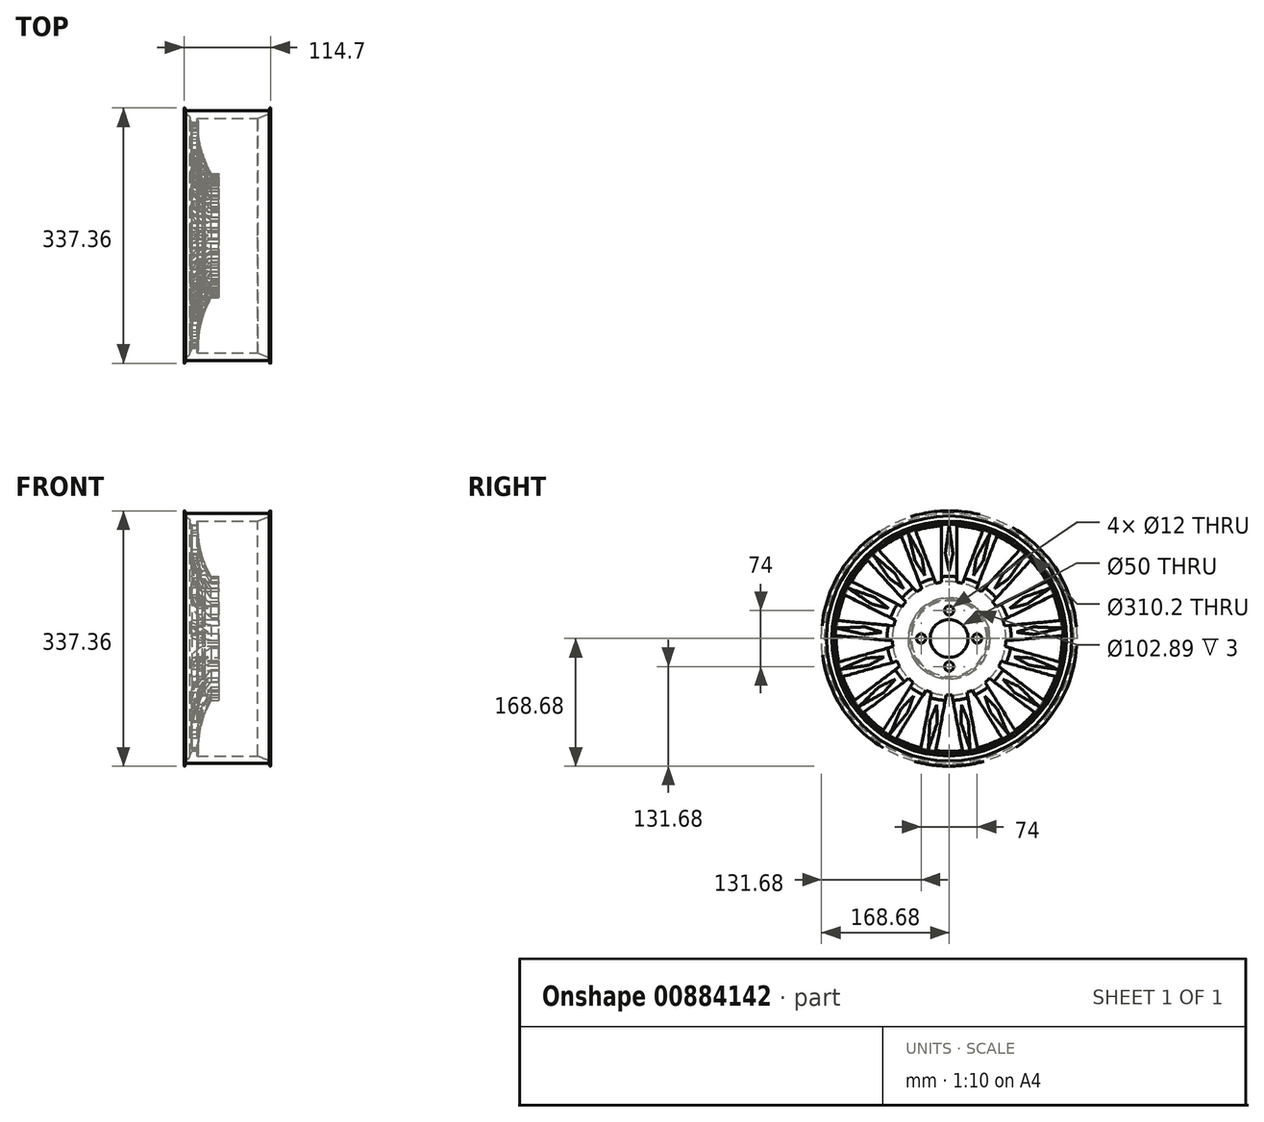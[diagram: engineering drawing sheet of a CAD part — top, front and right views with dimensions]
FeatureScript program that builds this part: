
annotation { "Feature Type Name" : "Feature", "Feature Type Description" : "" }
export const myFeature = defineFeature(function(context is Context, id is Id, definition is map)
    precondition{}
    {
        {
            var Q0;
            Q0=qCreatedBy(makeId("Front.planeOp"),FACE);
            var sketch = newSketch(context, id + "F0", { "sketchPlane" : qUnion([Q0])});
            skLineSegment(sketch, "E0", {"start": v(0, 0) * mm, "end": v(0, 165.1) * mm, "construction": true});
            skLineSegment(sketch, "E1", {"start": v(0, 0) * mm, "end": v(-35, 0) * mm, "construction": true});
            skLineSegment(sketch, "E2", {"start": v(0, 165.1) * mm, "end": v(-55, 165.1) * mm});
            skLineSegment(sketch, "E3", {"start": v(-35, 0) * mm, "end": v(-35, 25) * mm, "construction": true});
            skLineSegment(sketch, "E4", {"start": v(-35, 25) * mm, "end": v(-39.8, 25) * mm});
            skLineSegment(sketch, "E5", {"start": v(-40, 25.2) * mm, "end": v(-40, 49.8) * mm});
            skLineSegment(sketch, "E6", {"start": v(-39.8, 50) * mm, "end": v(-31.06, 50) * mm});
            skLineSegment(sketch, "E7", {"start": v(-55, 165.1) * mm, "end": v(-56.17, 168.55) * mm});
            skLineSegment(sketch, "E8", {"start": v(-56.39, 168.68) * mm, "end": v(-56.92, 168.6) * mm});
            skLineSegment(sketch, "E9", {"start": v(-57.34, 168.03) * mm, "end": v(-56.72, 163.88) * mm});
            skLineSegment(sketch, "E10", {"start": v(-56.67, 163.14) * mm, "end": v(-56.67, 162.14) * mm});
            skLineSegment(sketch, "E11", {"start": v(-56.41, 161.7) * mm, "end": v(-52.07, 159.23) * mm});
            skLineSegment(sketch, "E12", {"start": v(-49.55, 154.88) * mm, "end": v(-49.55, 153.88) * mm});
            skLineSegment(sketch, "E13", {"start": v(-49.16, 152.7) * mm, "end": v(-46.66, 149.26) * mm});
            skArc(sketch, "E14", {"start": v(-46.66, 149.26) * mm, "mid": v(-45.48, 111.09) * mm, "end": v(-32.98, 75) * mm});
            skPoint(sketch, "E15.visualSharp", {"position": v(-56.22, 168.7) * mm});
            skArc(sketch, "E15.filletArc", {"start": v(-56.17, 168.55) * mm, "mid": v(-56.25, 168.66) * mm, "end": v(-56.39, 168.68) * mm});
            skPoint(sketch, "E16.visualSharp", {"position": v(-57.42, 168.53) * mm});
            skArc(sketch, "E16.filletArc", {"start": v(-56.92, 168.6) * mm, "mid": v(-57.25, 168.4) * mm, "end": v(-57.34, 168.03) * mm});
            skPoint(sketch, "E17.visualSharp", {"position": v(-56.67, 163.51) * mm});
            skArc(sketch, "E17.filletArc", {"start": v(-56.67, 163.14) * mm, "mid": v(-56.68, 163.5) * mm, "end": v(-56.72, 163.88) * mm});
            skPoint(sketch, "E18.visualSharp", {"position": v(-56.67, 161.85) * mm});
            skArc(sketch, "E18.filletArc", {"start": v(-56.67, 162.14) * mm, "mid": v(-56.6, 161.89) * mm, "end": v(-56.41, 161.7) * mm});
            skPoint(sketch, "E19.visualSharp", {"position": v(-49.55, 157.79) * mm});
            skArc(sketch, "E19.filletArc", {"start": v(-49.55, 154.88) * mm, "mid": v(-50.22, 157.4) * mm, "end": v(-52.07, 159.23) * mm});
            skPoint(sketch, "E20.visualSharp", {"position": v(-49.55, 153.23) * mm});
            skArc(sketch, "E20.filletArc", {"start": v(-49.55, 153.88) * mm, "mid": v(-49.45, 153.26) * mm, "end": v(-49.16, 152.7) * mm});
            skPoint(sketch, "E21.visualSharp", {"position": v(-32.27, 50) * mm});
            skArc(sketch, "E21.filletArc", {"start": v(-31.06, 50) * mm, "mid": v(-29.86, 53.61) * mm, "end": v(-32.98, 51.45) * mm});
            skLineSegment(sketch, "E22", {"start": v(0, 155.1) * mm, "end": v(-40, 155.1) * mm});
            skLineSegment(sketch, "E23", {"start": v(-40, 155.1) * mm, "end": v(-39.2, 153.27) * mm});
            skLineSegment(sketch, "E24", {"start": v(-39.2, 153.27) * mm, "end": v(-38.39, 151.44) * mm});
            skLineSegment(sketch, "E25", {"start": v(-32.98, 75) * mm, "end": v(-29.98, 75) * mm});
            skLineSegment(sketch, "E26", {"start": v(-29.98, 75) * mm, "end": v(-29.98, 51.45) * mm});
            skLineSegment(sketch, "E27", {"start": v(-29.98, 51.45) * mm, "end": v(-32.98, 51.45) * mm});
            skLineSegment(sketch, "E28", {"start": v(-11.34, 82.01) * mm, "end": v(-11.34, 0) * mm});
            skLineSegment(sketch, "E29", {"start": v(-35, 25) * mm, "end": v(-11.34, 25) * mm});
            skLineSegment(sketch, "E30", {"start": v(-11.34, 82.01) * mm, "end": v(-21.34, 82.01) * mm});
            skArc(sketch, "E31", {"start": v(-38.39, 151.44) * mm, "mid": v(-34.96, 115.48) * mm, "end": v(-21.34, 82.01) * mm});
            skLineSegment(sketch, "E32.MirrorCS", {"start": v(0, 165.1) * mm, "end": v(55, 165.1) * mm});
            skLineSegment(sketch, "E33.MirrorCS", {"start": v(55, 165.1) * mm, "end": v(56.17, 168.55) * mm});
            skArc(sketch, "E34.MirrorCS", {"start": v(56.17, 168.55) * mm, "mid": v(56.25, 168.66) * mm, "end": v(56.39, 168.68) * mm});
            skLineSegment(sketch, "E35.MirrorCS", {"start": v(56.39, 168.68) * mm, "end": v(56.92, 168.6) * mm});
            skArc(sketch, "E36.MirrorCS", {"start": v(56.92, 168.6) * mm, "mid": v(57.25, 168.4) * mm, "end": v(57.34, 168.03) * mm});
            skLineSegment(sketch, "E37.MirrorCS", {"start": v(57.34, 168.03) * mm, "end": v(56.72, 163.88) * mm});
            skArc(sketch, "E38.MirrorCS", {"start": v(56.67, 163.14) * mm, "mid": v(56.68, 163.5) * mm, "end": v(56.72, 163.88) * mm});
            skLineSegment(sketch, "E39.MirrorCS", {"start": v(56.67, 163.14) * mm, "end": v(56.67, 162.14) * mm});
            skArc(sketch, "E40.MirrorCS", {"start": v(56.67, 162.14) * mm, "mid": v(56.65, 162) * mm, "end": v(56.6, 161.89) * mm});
            skLineSegment(sketch, "E41.MirrorCS", {"start": v(0, 155.1) * mm, "end": v(40, 155.1) * mm});
            skLineSegment(sketch, "E42", {"start": v(40, 155.1) * mm, "end": v(56.6, 161.89) * mm});
            skPoint(sketch, "E43.orphan", {"position": v(56.41, 161.7) * mm});
            skPoint(sketch, "E44.visualSharp", {"position": v(-40, 50) * mm});
            skArc(sketch, "E44.filletArc", {"start": v(-39.8, 50) * mm, "mid": v(-39.94, 49.95) * mm, "end": v(-40, 49.8) * mm});
            skPoint(sketch, "E45.visualSharp", {"position": v(-40, 25) * mm});
            skArc(sketch, "E45.filletArc", {"start": v(-40, 25.2) * mm, "mid": v(-39.94, 25.06) * mm, "end": v(-39.8, 25) * mm});
            skSolve(sketch);
        }
        {
            var Q0;
            Q0 = qSketchRegion(id + "F0", true);
            var Q1;
            Q1=sQuery(id+"F0.wireOp",EDGE,"E1");
            revolve(context, id + "F1", {"surfaceOperationType" : NewSurfaceOperationType.NEW, "entities" : qUnion([Q0]), "axis" : qUnion([Q1]), "revolveType" : RevolveType.FULL});
        }
        {
            var Q0;
            Q0=makeQuery(id+"F1.opRevolve","SWEPT_FACE",FACE,{"disambiguationData":[OSD([sQuery(id+"F0.wireOp",EDGE,"E5")])]});
            var sketch = newSketch(context, id + "F2", { "sketchPlane" : qUnion([Q0])});
            skLineSegment(sketch, "E46", {"start": v(0, 89.26) * mm, "end": v(0, 149.26) * mm, "construction": true});
            skLineSegment(sketch, "E47", {"start": v(10, 74.33) * mm, "end": v(10, 148.93) * mm});
            skLineSegment(sketch, "E48.MirrorCS", {"start": v(-10, 74.33) * mm, "end": v(-10, 148.93) * mm});
            skLineSegment(sketch, "E49", {"start": v(5, 79.84) * mm, "end": v(5, 144.18) * mm, "construction": true});
            skLineSegment(sketch, "E50.MirrorCS", {"start": v(-5, 79.84) * mm, "end": v(-5, 144.18) * mm, "construction": true});
            skLineSegment(sketch, "E51", {"start": v(0, 89.26) * mm, "end": v(5, 112.01) * mm});
            skLineSegment(sketch, "E52", {"start": v(5, 112.01) * mm, "end": v(0, 149.26) * mm});
            skLineSegment(sketch, "E53", {"start": v(0, 89.26) * mm, "end": v(-5, 112.01) * mm});
            skLineSegment(sketch, "E54", {"start": v(-5, 112.01) * mm, "end": v(0, 149.26) * mm});
            skCircle(sketch, "E55", {"center": v(0, 0) * mm, "radius": 75 * mm});
            skCircle(sketch, "E56", {"center": v(0, 0) * mm, "radius": 149.26 * mm});
            skLineSegment(sketch, "E57.1.0", {"start": v(-36.18, 65.7) * mm, "end": v(-63.12, 135.26) * mm});
            skLineSegment(sketch, "E57.1.1", {"start": v(-35.8, 106.25) * mm, "end": v(-53.92, 139.18) * mm});
            skLineSegment(sketch, "E57.1.2", {"start": v(-32.25, 83.24) * mm, "end": v(-35.8, 106.25) * mm});
            skLineSegment(sketch, "E57.1.3", {"start": v(-32.25, 83.24) * mm, "end": v(-45.13, 102.64) * mm});
            skLineSegment(sketch, "E57.1.4", {"start": v(-45.13, 102.64) * mm, "end": v(-53.92, 139.18) * mm});
            skLineSegment(sketch, "E57.1.5", {"start": v(-17.53, 72.92) * mm, "end": v(-44.47, 142.48) * mm});
            skLineSegment(sketch, "E57.2.0", {"start": v(-57.47, 48.2) * mm, "end": v(-107.72, 103.32) * mm});
            skLineSegment(sketch, "E57.2.1", {"start": v(-71.77, 86.15) * mm, "end": v(-100.56, 110.3) * mm});
            skLineSegment(sketch, "E57.2.2", {"start": v(-60.14, 65.97) * mm, "end": v(-71.77, 86.15) * mm});
            skLineSegment(sketch, "E57.2.3", {"start": v(-60.14, 65.97) * mm, "end": v(-79.16, 79.4) * mm});
            skLineSegment(sketch, "E57.2.4", {"start": v(-79.16, 79.4) * mm, "end": v(-100.56, 110.3) * mm});
            skLineSegment(sketch, "E57.2.5", {"start": v(-42.69, 61.67) * mm, "end": v(-92.94, 116.8) * mm});
            skLineSegment(sketch, "E57.3.0", {"start": v(-71, 24.18) * mm, "end": v(-137.77, 57.43) * mm});
            skLineSegment(sketch, "E57.3.1", {"start": v(-98.04, 54.4) * mm, "end": v(-133.62, 66.53) * mm});
            skLineSegment(sketch, "E57.3.2", {"start": v(-79.9, 39.79) * mm, "end": v(-98.04, 54.4) * mm});
            skLineSegment(sketch, "E57.3.3", {"start": v(-79.9, 39.79) * mm, "end": v(-102.5, 45.45) * mm});
            skLineSegment(sketch, "E57.3.4", {"start": v(-102.5, 45.45) * mm, "end": v(-133.62, 66.53) * mm});
            skLineSegment(sketch, "E57.3.5", {"start": v(-62.08, 42.08) * mm, "end": v(-128.86, 75.33) * mm});
            skLineSegment(sketch, "E57.4.0", {"start": v(-74.94, -3.1) * mm, "end": v(-149.22, 3.78) * mm});
            skLineSegment(sketch, "E57.4.1", {"start": v(-111.07, 15.31) * mm, "end": v(-148.63, 13.77) * mm});
            skLineSegment(sketch, "E57.4.2", {"start": v(-88.88, 8.24) * mm, "end": v(-111.07, 15.31) * mm});
            skLineSegment(sketch, "E57.4.3", {"start": v(-88.88, 8.24) * mm, "end": v(-112, 5.36) * mm});
            skLineSegment(sketch, "E57.4.4", {"start": v(-112, 5.36) * mm, "end": v(-148.63, 13.77) * mm});
            skLineSegment(sketch, "E57.4.5", {"start": v(-73.1, 16.82) * mm, "end": v(-147.37, 23.7) * mm});
            skLineSegment(sketch, "E57.5.0", {"start": v(-68.76, -29.96) * mm, "end": v(-140.5, -50.37) * mm});
            skLineSegment(sketch, "E57.5.1", {"start": v(-109.1, -25.84) * mm, "end": v(-143.57, -40.85) * mm});
            skLineSegment(sketch, "E57.5.2", {"start": v(-85.86, -24.43) * mm, "end": v(-109.1, -25.84) * mm});
            skLineSegment(sketch, "E57.5.3", {"start": v(-85.86, -24.43) * mm, "end": v(-106.37, -35.46) * mm});
            skLineSegment(sketch, "E57.5.4", {"start": v(-106.37, -35.46) * mm, "end": v(-143.57, -40.85) * mm});
            skLineSegment(sketch, "E57.5.5", {"start": v(-74.23, -10.72) * mm, "end": v(-145.98, -31.14) * mm});
            skLineSegment(sketch, "E57.6.0", {"start": v(-53.3, -52.77) * mm, "end": v(-112.82, -97.73) * mm});
            skLineSegment(sketch, "E57.6.1", {"start": v(-92.4, -63.51) * mm, "end": v(-119.12, -89.95) * mm});
            skLineSegment(sketch, "E57.6.2", {"start": v(-71.23, -53.8) * mm, "end": v(-92.4, -63.51) * mm});
            skLineSegment(sketch, "E57.6.3", {"start": v(-71.23, -53.8) * mm, "end": v(-86.37, -71.5) * mm});
            skLineSegment(sketch, "E57.6.4", {"start": v(-86.37, -71.5) * mm, "end": v(-119.12, -89.95) * mm});
            skLineSegment(sketch, "E57.6.5", {"start": v(-65.34, -36.81) * mm, "end": v(-124.87, -81.77) * mm});
            skLineSegment(sketch, "E57.7.0", {"start": v(-30.63, -68.46) * mm, "end": v(-69.9, -131.89) * mm});
            skLineSegment(sketch, "E57.7.1", {"start": v(-63.22, -92.6) * mm, "end": v(-78.58, -126.9) * mm});
            skLineSegment(sketch, "E57.7.2", {"start": v(-47, -75.9) * mm, "end": v(-63.22, -92.6) * mm});
            skLineSegment(sketch, "E57.7.3", {"start": v(-47, -75.9) * mm, "end": v(-54.71, -97.87) * mm});
            skLineSegment(sketch, "E57.7.4", {"start": v(-54.71, -97.87) * mm, "end": v(-78.58, -126.9) * mm});
            skLineSegment(sketch, "E57.7.5", {"start": v(-47.63, -57.93) * mm, "end": v(-86.9, -121.36) * mm});
            skLineSegment(sketch, "E57.8.0", {"start": v(-3.83, -74.9) * mm, "end": v(-17.54, -148.23) * mm});
            skLineSegment(sketch, "E57.8.1", {"start": v(-25.5, -109.18) * mm, "end": v(-27.43, -146.72) * mm});
            skLineSegment(sketch, "E57.8.2", {"start": v(-16.4, -87.74) * mm, "end": v(-25.5, -109.18) * mm});
            skLineSegment(sketch, "E57.8.3", {"start": v(-16.4, -87.74) * mm, "end": v(-15.67, -111.02) * mm});
            skLineSegment(sketch, "E57.8.4", {"start": v(-15.67, -111.02) * mm, "end": v(-27.43, -146.72) * mm});
            skLineSegment(sketch, "E57.8.5", {"start": v(-23.49, -71.23) * mm, "end": v(-37.2, -144.56) * mm});
            skLineSegment(sketch, "E57.9.0", {"start": v(23.49, -71.23) * mm, "end": v(37.2, -144.56) * mm});
            skLineSegment(sketch, "E57.9.1", {"start": v(15.67, -111.02) * mm, "end": v(27.43, -146.72) * mm});
            skLineSegment(sketch, "E57.9.2", {"start": v(16.4, -87.74) * mm, "end": v(15.67, -111.02) * mm});
            skLineSegment(sketch, "E57.9.3", {"start": v(16.4, -87.74) * mm, "end": v(25.5, -109.18) * mm});
            skLineSegment(sketch, "E57.9.4", {"start": v(25.5, -109.18) * mm, "end": v(27.43, -146.72) * mm});
            skLineSegment(sketch, "E57.9.5", {"start": v(3.83, -74.9) * mm, "end": v(17.54, -148.23) * mm});
            skLineSegment(sketch, "E57.10.0", {"start": v(47.63, -57.93) * mm, "end": v(86.9, -121.36) * mm});
            skLineSegment(sketch, "E57.10.1", {"start": v(54.71, -97.87) * mm, "end": v(78.58, -126.9) * mm});
            skLineSegment(sketch, "E57.10.2", {"start": v(47, -75.9) * mm, "end": v(54.71, -97.87) * mm});
            skLineSegment(sketch, "E57.10.3", {"start": v(47, -75.9) * mm, "end": v(63.22, -92.6) * mm});
            skLineSegment(sketch, "E57.10.4", {"start": v(63.22, -92.6) * mm, "end": v(78.58, -126.9) * mm});
            skLineSegment(sketch, "E57.10.5", {"start": v(30.63, -68.46) * mm, "end": v(69.9, -131.89) * mm});
            skLineSegment(sketch, "E57.11.0", {"start": v(65.34, -36.81) * mm, "end": v(124.87, -81.77) * mm});
            skLineSegment(sketch, "E57.11.1", {"start": v(86.37, -71.5) * mm, "end": v(119.12, -89.95) * mm});
            skLineSegment(sketch, "E57.11.2", {"start": v(71.23, -53.8) * mm, "end": v(86.37, -71.5) * mm});
            skLineSegment(sketch, "E57.11.3", {"start": v(71.23, -53.8) * mm, "end": v(92.4, -63.51) * mm});
            skLineSegment(sketch, "E57.11.4", {"start": v(92.4, -63.51) * mm, "end": v(119.12, -89.95) * mm});
            skLineSegment(sketch, "E57.11.5", {"start": v(53.3, -52.77) * mm, "end": v(112.82, -97.73) * mm});
            skLineSegment(sketch, "E57.12.0", {"start": v(74.23, -10.72) * mm, "end": v(145.98, -31.14) * mm});
            skLineSegment(sketch, "E57.12.1", {"start": v(106.37, -35.46) * mm, "end": v(143.57, -40.85) * mm});
            skLineSegment(sketch, "E57.12.2", {"start": v(85.86, -24.43) * mm, "end": v(106.37, -35.46) * mm});
            skLineSegment(sketch, "E57.12.3", {"start": v(85.86, -24.43) * mm, "end": v(109.1, -25.84) * mm});
            skLineSegment(sketch, "E57.12.4", {"start": v(109.1, -25.84) * mm, "end": v(143.57, -40.85) * mm});
            skLineSegment(sketch, "E57.12.5", {"start": v(68.76, -29.96) * mm, "end": v(140.5, -50.37) * mm});
            skLineSegment(sketch, "E57.13.0", {"start": v(73.1, 16.82) * mm, "end": v(147.37, 23.7) * mm});
            skLineSegment(sketch, "E57.13.1", {"start": v(112, 5.36) * mm, "end": v(148.63, 13.77) * mm});
            skLineSegment(sketch, "E57.13.2", {"start": v(88.88, 8.24) * mm, "end": v(112, 5.36) * mm});
            skLineSegment(sketch, "E57.13.3", {"start": v(88.88, 8.24) * mm, "end": v(111.07, 15.31) * mm});
            skLineSegment(sketch, "E57.13.4", {"start": v(111.07, 15.31) * mm, "end": v(148.63, 13.77) * mm});
            skLineSegment(sketch, "E57.13.5", {"start": v(74.94, -3.1) * mm, "end": v(149.22, 3.78) * mm});
            skLineSegment(sketch, "E57.14.0", {"start": v(62.08, 42.08) * mm, "end": v(128.86, 75.33) * mm});
            skLineSegment(sketch, "E57.14.1", {"start": v(102.5, 45.45) * mm, "end": v(133.62, 66.53) * mm});
            skLineSegment(sketch, "E57.14.2", {"start": v(79.9, 39.79) * mm, "end": v(102.5, 45.45) * mm});
            skLineSegment(sketch, "E57.14.3", {"start": v(79.9, 39.79) * mm, "end": v(98.04, 54.4) * mm});
            skLineSegment(sketch, "E57.14.4", {"start": v(98.04, 54.4) * mm, "end": v(133.62, 66.53) * mm});
            skLineSegment(sketch, "E57.14.5", {"start": v(71, 24.18) * mm, "end": v(137.77, 57.43) * mm});
            skLineSegment(sketch, "E57.15.0", {"start": v(42.69, 61.67) * mm, "end": v(92.94, 116.8) * mm});
            skLineSegment(sketch, "E57.15.1", {"start": v(79.16, 79.4) * mm, "end": v(100.56, 110.3) * mm});
            skLineSegment(sketch, "E57.15.2", {"start": v(60.14, 65.97) * mm, "end": v(79.16, 79.4) * mm});
            skLineSegment(sketch, "E57.15.3", {"start": v(60.14, 65.97) * mm, "end": v(71.77, 86.15) * mm});
            skLineSegment(sketch, "E57.15.4", {"start": v(71.77, 86.15) * mm, "end": v(100.56, 110.3) * mm});
            skLineSegment(sketch, "E57.15.5", {"start": v(57.47, 48.2) * mm, "end": v(107.72, 103.32) * mm});
            skLineSegment(sketch, "E57.16.0", {"start": v(17.53, 72.92) * mm, "end": v(44.47, 142.48) * mm});
            skLineSegment(sketch, "E57.16.1", {"start": v(45.13, 102.64) * mm, "end": v(53.92, 139.18) * mm});
            skLineSegment(sketch, "E57.16.2", {"start": v(32.25, 83.24) * mm, "end": v(45.13, 102.64) * mm});
            skLineSegment(sketch, "E57.16.3", {"start": v(32.25, 83.24) * mm, "end": v(35.8, 106.25) * mm});
            skLineSegment(sketch, "E57.16.4", {"start": v(35.8, 106.25) * mm, "end": v(53.92, 139.18) * mm});
            skLineSegment(sketch, "E57.16.5", {"start": v(36.18, 65.7) * mm, "end": v(63.12, 135.26) * mm});
            skSolve(sketch);
        }
        {
            var Q0;
            {var subQ0=sQuery(id+"F2.wireOp",EDGE,"E57.2.0");Q0=makeQuery(id+"F2.imprint","IMPRINT",FACE,{"disambiguationData":[TD([[makeQuery(id+"F2.imprint","IMPRINT",EDGE,{"derivedFrom":subQ0}),1.0]])]});}
            var Q1;
            {var subQ0=sQuery(id+"F2.wireOp",EDGE,"E57.1.0");Q1=makeQuery(id+"F2.imprint","IMPRINT",FACE,{"disambiguationData":[TD([[makeQuery(id+"F2.imprint","IMPRINT",EDGE,{"derivedFrom":subQ0}),1.0]])]});}
            var Q2;
            {var subQ0=sQuery(id+"F2.wireOp",EDGE,"E48.MirrorCS");Q2=makeQuery(id+"F2.imprint","IMPRINT",FACE,{"disambiguationData":[TD([[makeQuery(id+"F2.imprint","IMPRINT",EDGE,{"derivedFrom":subQ0}),1.0]])]});}
            var Q3;
            {var subQ0=sQuery(id+"F2.wireOp",EDGE,"E47");Q3=makeQuery(id+"F2.imprint","IMPRINT",FACE,{"disambiguationData":[TD([[makeQuery(id+"F2.imprint","IMPRINT",EDGE,{"derivedFrom":subQ0}),-1.0]])]});}
            var Q4;
            {var subQ0=sQuery(id+"F2.wireOp",EDGE,"E57.15.0");Q4=makeQuery(id+"F2.imprint","IMPRINT",FACE,{"disambiguationData":[TD([[makeQuery(id+"F2.imprint","IMPRINT",EDGE,{"derivedFrom":subQ0}),1.0]])]});}
            var Q5;
            {var subQ0=sQuery(id+"F2.wireOp",EDGE,"E57.14.0");Q5=makeQuery(id+"F2.imprint","IMPRINT",FACE,{"disambiguationData":[TD([[makeQuery(id+"F2.imprint","IMPRINT",EDGE,{"derivedFrom":subQ0}),1.0]])]});}
            var Q6;
            {var subQ0=sQuery(id+"F2.wireOp",EDGE,"E57.3.0");Q6=makeQuery(id+"F2.imprint","IMPRINT",FACE,{"disambiguationData":[TD([[makeQuery(id+"F2.imprint","IMPRINT",EDGE,{"derivedFrom":subQ0}),1.0]])]});}
            var Q7;
            {var subQ0=sQuery(id+"F2.wireOp",EDGE,"E57.4.0");Q7=makeQuery(id+"F2.imprint","IMPRINT",FACE,{"disambiguationData":[TD([[makeQuery(id+"F2.imprint","IMPRINT",EDGE,{"derivedFrom":subQ0}),1.0]])]});}
            var Q8;
            {var subQ0=sQuery(id+"F2.wireOp",EDGE,"E57.5.0");Q8=makeQuery(id+"F2.imprint","IMPRINT",FACE,{"disambiguationData":[TD([[makeQuery(id+"F2.imprint","IMPRINT",EDGE,{"derivedFrom":subQ0}),1.0]])]});}
            var Q9;
            {var subQ0=sQuery(id+"F2.wireOp",EDGE,"E57.6.0");Q9=makeQuery(id+"F2.imprint","IMPRINT",FACE,{"disambiguationData":[TD([[makeQuery(id+"F2.imprint","IMPRINT",EDGE,{"derivedFrom":subQ0}),1.0]])]});}
            var Q10;
            {var subQ0=sQuery(id+"F2.wireOp",EDGE,"E57.7.0");Q10=makeQuery(id+"F2.imprint","IMPRINT",FACE,{"disambiguationData":[TD([[makeQuery(id+"F2.imprint","IMPRINT",EDGE,{"derivedFrom":subQ0}),1.0]])]});}
            var Q11;
            {var subQ0=sQuery(id+"F2.wireOp",EDGE,"E57.8.0");Q11=makeQuery(id+"F2.imprint","IMPRINT",FACE,{"disambiguationData":[TD([[makeQuery(id+"F2.imprint","IMPRINT",EDGE,{"derivedFrom":subQ0}),1.0]])]});}
            var Q12;
            {var subQ0=sQuery(id+"F2.wireOp",EDGE,"E57.9.0");Q12=makeQuery(id+"F2.imprint","IMPRINT",FACE,{"disambiguationData":[TD([[makeQuery(id+"F2.imprint","IMPRINT",EDGE,{"derivedFrom":subQ0}),1.0]])]});}
            var Q13;
            {var subQ0=sQuery(id+"F2.wireOp",EDGE,"E57.10.0");Q13=makeQuery(id+"F2.imprint","IMPRINT",FACE,{"disambiguationData":[TD([[makeQuery(id+"F2.imprint","IMPRINT",EDGE,{"derivedFrom":subQ0}),1.0]])]});}
            var Q14;
            {var subQ0=sQuery(id+"F2.wireOp",EDGE,"E57.11.0");Q14=makeQuery(id+"F2.imprint","IMPRINT",FACE,{"disambiguationData":[TD([[makeQuery(id+"F2.imprint","IMPRINT",EDGE,{"derivedFrom":subQ0}),1.0]])]});}
            var Q15;
            {var subQ0=sQuery(id+"F2.wireOp",EDGE,"E57.12.0");Q15=makeQuery(id+"F2.imprint","IMPRINT",FACE,{"disambiguationData":[TD([[makeQuery(id+"F2.imprint","IMPRINT",EDGE,{"derivedFrom":subQ0}),1.0]])]});}
            var Q16;
            {var subQ0=sQuery(id+"F2.wireOp",EDGE,"E57.13.0");Q16=makeQuery(id+"F2.imprint","IMPRINT",FACE,{"disambiguationData":[TD([[makeQuery(id+"F2.imprint","IMPRINT",EDGE,{"derivedFrom":subQ0}),1.0]])]});}
            extrude(context, id + "F3", {"entities" : qUnion([Q0, Q1, Q2, Q3, Q4, Q5, Q6, Q7, Q8, Q9, Q10, Q11, Q12, Q13, Q14, Q15, Q16]), "operationType" : NewBodyOperationType.REMOVE, "oppositeDirection" : true, "depth" : 200 * mm, "offsetDistance" : 25 * mm});
        }
        {
            var Q0;
            Q0=makeQuery(id+"F2.imprint","IMPRINT",FACE,{"disambiguationData":[TD([[makeQuery(id+"F2.imprint","IMPRINT",EDGE,{"derivedFrom":sQuery(id+"F2.wireOp",EDGE,"E57.1.1")}),1.0]])]});
            var Q1;
            Q1=makeQuery(id+"F2.imprint","IMPRINT",FACE,{"disambiguationData":[TD([[makeQuery(id+"F2.imprint","IMPRINT",EDGE,{"derivedFrom":sQuery(id+"F2.wireOp",EDGE,"E51")}),1.0]])]});
            var Q2;
            Q2=makeQuery(id+"F2.imprint","IMPRINT",FACE,{"disambiguationData":[TD([[makeQuery(id+"F2.imprint","IMPRINT",EDGE,{"derivedFrom":sQuery(id+"F2.wireOp",EDGE,"E57.2.1")}),1.0]])]});
            var Q3;
            Q3=makeQuery(id+"F2.imprint","IMPRINT",FACE,{"disambiguationData":[TD([[makeQuery(id+"F2.imprint","IMPRINT",EDGE,{"derivedFrom":sQuery(id+"F2.wireOp",EDGE,"E57.3.1")}),1.0]])]});
            var Q4;
            Q4=makeQuery(id+"F2.imprint","IMPRINT",FACE,{"disambiguationData":[TD([[makeQuery(id+"F2.imprint","IMPRINT",EDGE,{"derivedFrom":sQuery(id+"F2.wireOp",EDGE,"E57.4.1")}),1.0]])]});
            var Q5;
            Q5=makeQuery(id+"F2.imprint","IMPRINT",FACE,{"disambiguationData":[TD([[makeQuery(id+"F2.imprint","IMPRINT",EDGE,{"derivedFrom":sQuery(id+"F2.wireOp",EDGE,"E57.5.1")}),1.0]])]});
            var Q6;
            Q6=makeQuery(id+"F2.imprint","IMPRINT",FACE,{"disambiguationData":[TD([[makeQuery(id+"F2.imprint","IMPRINT",EDGE,{"derivedFrom":sQuery(id+"F2.wireOp",EDGE,"E57.6.1")}),1.0]])]});
            var Q7;
            Q7=makeQuery(id+"F2.imprint","IMPRINT",FACE,{"disambiguationData":[TD([[makeQuery(id+"F2.imprint","IMPRINT",EDGE,{"derivedFrom":sQuery(id+"F2.wireOp",EDGE,"E57.7.1")}),1.0]])]});
            var Q8;
            Q8=makeQuery(id+"F2.imprint","IMPRINT",FACE,{"disambiguationData":[TD([[makeQuery(id+"F2.imprint","IMPRINT",EDGE,{"derivedFrom":sQuery(id+"F2.wireOp",EDGE,"E57.8.1")}),1.0]])]});
            var Q9;
            Q9=makeQuery(id+"F2.imprint","IMPRINT",FACE,{"disambiguationData":[TD([[makeQuery(id+"F2.imprint","IMPRINT",EDGE,{"derivedFrom":sQuery(id+"F2.wireOp",EDGE,"E57.9.1")}),1.0]])]});
            var Q10;
            Q10=makeQuery(id+"F2.imprint","IMPRINT",FACE,{"disambiguationData":[TD([[makeQuery(id+"F2.imprint","IMPRINT",EDGE,{"derivedFrom":sQuery(id+"F2.wireOp",EDGE,"E57.10.1")}),1.0]])]});
            var Q11;
            Q11=makeQuery(id+"F2.imprint","IMPRINT",FACE,{"disambiguationData":[TD([[makeQuery(id+"F2.imprint","IMPRINT",EDGE,{"derivedFrom":sQuery(id+"F2.wireOp",EDGE,"E57.11.1")}),1.0]])]});
            var Q12;
            Q12=makeQuery(id+"F2.imprint","IMPRINT",FACE,{"disambiguationData":[TD([[makeQuery(id+"F2.imprint","IMPRINT",EDGE,{"derivedFrom":sQuery(id+"F2.wireOp",EDGE,"E57.12.1")}),1.0]])]});
            var Q13;
            Q13=makeQuery(id+"F2.imprint","IMPRINT",FACE,{"disambiguationData":[TD([[makeQuery(id+"F2.imprint","IMPRINT",EDGE,{"derivedFrom":sQuery(id+"F2.wireOp",EDGE,"E57.13.1")}),1.0]])]});
            var Q14;
            Q14=makeQuery(id+"F2.imprint","IMPRINT",FACE,{"disambiguationData":[TD([[makeQuery(id+"F2.imprint","IMPRINT",EDGE,{"derivedFrom":sQuery(id+"F2.wireOp",EDGE,"E57.16.1")}),1.0]])]});
            var Q15;
            Q15=makeQuery(id+"F2.imprint","IMPRINT",FACE,{"disambiguationData":[TD([[makeQuery(id+"F2.imprint","IMPRINT",EDGE,{"derivedFrom":sQuery(id+"F2.wireOp",EDGE,"E57.15.1")}),1.0]])]});
            var Q16;
            Q16=makeQuery(id+"F2.imprint","IMPRINT",FACE,{"disambiguationData":[TD([[makeQuery(id+"F2.imprint","IMPRINT",EDGE,{"derivedFrom":sQuery(id+"F2.wireOp",EDGE,"E57.14.1")}),1.0]])]});
            extrude(context, id + "F4", {"entities" : qUnion([Q0, Q1, Q2, Q3, Q4, Q5, Q6, Q7, Q8, Q9, Q10, Q11, Q12, Q13, Q14, Q15, Q16]), "operationType" : NewBodyOperationType.REMOVE, "oppositeDirection" : true, "depth" : 200 * mm, "offsetDistance" : 25 * mm});
        }
        {
            var Q0;
            Q0=makeQuery(id+"F3.boolean.opBoolean","COPY",FACE,{"derivedFrom":makeQuery(id+"F3.opExtrude","CAP_FACE",FACE,{"disambiguationData":[OSD([sQuery(id+"F2.wireOp",EDGE,"E55"),sQuery(id+"F2.wireOp",EDGE,"E56"),sQuery(id+"F2.wireOp",EDGE,"E57.1.0"),sQuery(id+"F2.wireOp",EDGE,"E57.2.5")])],"isStart":true})});
            var Q1;
            Q1=makeQuery(id+"F3.boolean.opBoolean","COPY",FACE,{"derivedFrom":makeQuery(id+"F3.opExtrude","CAP_FACE",FACE,{"disambiguationData":[OSD([sQuery(id+"F2.wireOp",EDGE,"E55"),sQuery(id+"F2.wireOp",EDGE,"E56"),sQuery(id+"F2.wireOp",EDGE,"E57.2.0"),sQuery(id+"F2.wireOp",EDGE,"E57.3.5")])],"isStart":true})});
            var Q2;
            Q2=makeQuery(id+"F3.boolean.opBoolean","COPY",FACE,{"derivedFrom":makeQuery(id+"F3.opExtrude","CAP_FACE",FACE,{"disambiguationData":[OSD([sQuery(id+"F2.wireOp",EDGE,"E55"),sQuery(id+"F2.wireOp",EDGE,"E56"),sQuery(id+"F2.wireOp",EDGE,"E57.3.0"),sQuery(id+"F2.wireOp",EDGE,"E57.4.5")])],"isStart":true})});
            var Q3;
            Q3=makeQuery(id+"F3.boolean.opBoolean","COPY",FACE,{"derivedFrom":makeQuery(id+"F3.opExtrude","CAP_FACE",FACE,{"disambiguationData":[OSD([sQuery(id+"F2.wireOp",EDGE,"E55"),sQuery(id+"F2.wireOp",EDGE,"E56"),sQuery(id+"F2.wireOp",EDGE,"E57.4.0"),sQuery(id+"F2.wireOp",EDGE,"E57.5.5")])],"isStart":true})});
            var Q4;
            Q4=makeQuery(id+"F3.boolean.opBoolean","COPY",FACE,{"derivedFrom":makeQuery(id+"F3.opExtrude","CAP_FACE",FACE,{"disambiguationData":[OSD([sQuery(id+"F2.wireOp",EDGE,"E55"),sQuery(id+"F2.wireOp",EDGE,"E56"),sQuery(id+"F2.wireOp",EDGE,"E57.5.0"),sQuery(id+"F2.wireOp",EDGE,"E57.6.5")])],"isStart":true})});
            var Q5;
            Q5=makeQuery(id+"F3.boolean.opBoolean","COPY",FACE,{"derivedFrom":makeQuery(id+"F3.opExtrude","CAP_FACE",FACE,{"disambiguationData":[OSD([sQuery(id+"F2.wireOp",EDGE,"E55"),sQuery(id+"F2.wireOp",EDGE,"E56"),sQuery(id+"F2.wireOp",EDGE,"E57.6.0"),sQuery(id+"F2.wireOp",EDGE,"E57.7.5")])],"isStart":true})});
            var Q6;
            Q6=makeQuery(id+"F3.boolean.opBoolean","COPY",FACE,{"derivedFrom":makeQuery(id+"F3.opExtrude","CAP_FACE",FACE,{"disambiguationData":[OSD([sQuery(id+"F2.wireOp",EDGE,"E55"),sQuery(id+"F2.wireOp",EDGE,"E56"),sQuery(id+"F2.wireOp",EDGE,"E57.7.0"),sQuery(id+"F2.wireOp",EDGE,"E57.8.5")])],"isStart":true})});
            var Q7;
            Q7=makeQuery(id+"F3.boolean.opBoolean","COPY",FACE,{"derivedFrom":makeQuery(id+"F3.opExtrude","CAP_FACE",FACE,{"disambiguationData":[OSD([sQuery(id+"F2.wireOp",EDGE,"E55"),sQuery(id+"F2.wireOp",EDGE,"E56"),sQuery(id+"F2.wireOp",EDGE,"E57.8.0"),sQuery(id+"F2.wireOp",EDGE,"E57.9.5")])],"isStart":true})});
            var Q8;
            Q8=makeQuery(id+"F3.boolean.opBoolean","COPY",FACE,{"derivedFrom":makeQuery(id+"F3.opExtrude","CAP_FACE",FACE,{"disambiguationData":[OSD([sQuery(id+"F2.wireOp",EDGE,"E55"),sQuery(id+"F2.wireOp",EDGE,"E56"),sQuery(id+"F2.wireOp",EDGE,"E57.9.0"),sQuery(id+"F2.wireOp",EDGE,"E57.10.5")])],"isStart":true})});
            var Q9;
            Q9=makeQuery(id+"F3.boolean.opBoolean","COPY",FACE,{"derivedFrom":makeQuery(id+"F3.opExtrude","CAP_FACE",FACE,{"disambiguationData":[OSD([sQuery(id+"F2.wireOp",EDGE,"E55"),sQuery(id+"F2.wireOp",EDGE,"E56"),sQuery(id+"F2.wireOp",EDGE,"E57.10.0"),sQuery(id+"F2.wireOp",EDGE,"E57.11.5")])],"isStart":true})});
            var Q10;
            Q10=makeQuery(id+"F3.boolean.opBoolean","COPY",FACE,{"derivedFrom":makeQuery(id+"F3.opExtrude","CAP_FACE",FACE,{"disambiguationData":[OSD([sQuery(id+"F2.wireOp",EDGE,"E55"),sQuery(id+"F2.wireOp",EDGE,"E56"),sQuery(id+"F2.wireOp",EDGE,"E57.11.0"),sQuery(id+"F2.wireOp",EDGE,"E57.12.5")])],"isStart":true})});
            var Q11;
            Q11=makeQuery(id+"F3.boolean.opBoolean","COPY",FACE,{"derivedFrom":makeQuery(id+"F3.opExtrude","CAP_FACE",FACE,{"disambiguationData":[OSD([sQuery(id+"F2.wireOp",EDGE,"E55"),sQuery(id+"F2.wireOp",EDGE,"E56"),sQuery(id+"F2.wireOp",EDGE,"E57.12.0"),sQuery(id+"F2.wireOp",EDGE,"E57.13.5")])],"isStart":true})});
            var Q12;
            Q12=makeQuery(id+"F3.boolean.opBoolean","COPY",FACE,{"derivedFrom":makeQuery(id+"F3.opExtrude","CAP_FACE",FACE,{"disambiguationData":[OSD([sQuery(id+"F2.wireOp",EDGE,"E55"),sQuery(id+"F2.wireOp",EDGE,"E56"),sQuery(id+"F2.wireOp",EDGE,"E57.13.0"),sQuery(id+"F2.wireOp",EDGE,"E57.14.5")])],"isStart":true})});
            var Q13;
            Q13=makeQuery(id+"F3.boolean.opBoolean","COPY",FACE,{"derivedFrom":makeQuery(id+"F3.opExtrude","CAP_FACE",FACE,{"disambiguationData":[OSD([sQuery(id+"F2.wireOp",EDGE,"E55"),sQuery(id+"F2.wireOp",EDGE,"E56"),sQuery(id+"F2.wireOp",EDGE,"E57.14.0"),sQuery(id+"F2.wireOp",EDGE,"E57.15.5")])],"isStart":true})});
            var Q14;
            Q14=makeQuery(id+"F3.boolean.opBoolean","COPY",FACE,{"derivedFrom":makeQuery(id+"F3.opExtrude","CAP_FACE",FACE,{"disambiguationData":[OSD([sQuery(id+"F2.wireOp",EDGE,"E55"),sQuery(id+"F2.wireOp",EDGE,"E56"),sQuery(id+"F2.wireOp",EDGE,"E57.15.0"),sQuery(id+"F2.wireOp",EDGE,"E57.16.5")])],"isStart":true})});
            var Q15;
            Q15=makeQuery(id+"F3.boolean.opBoolean","COPY",FACE,{"derivedFrom":makeQuery(id+"F3.opExtrude","CAP_FACE",FACE,{"disambiguationData":[OSD([sQuery(id+"F2.wireOp",EDGE,"E47"),sQuery(id+"F2.wireOp",EDGE,"E55"),sQuery(id+"F2.wireOp",EDGE,"E56"),sQuery(id+"F2.wireOp",EDGE,"E57.16.0")])],"isStart":true})});
            var Q16;
            Q16=makeQuery(id+"F3.boolean.opBoolean","COPY",FACE,{"derivedFrom":makeQuery(id+"F3.opExtrude","CAP_FACE",FACE,{"disambiguationData":[OSD([sQuery(id+"F2.wireOp",EDGE,"E48.MirrorCS"),sQuery(id+"F2.wireOp",EDGE,"E55"),sQuery(id+"F2.wireOp",EDGE,"E56"),sQuery(id+"F2.wireOp",EDGE,"E57.1.5")])],"isStart":true})});
            extrude(context, id + "F5", {"entities" : qUnion([Q0, Q1, Q2, Q3, Q4, Q5, Q6, Q7, Q8, Q9, Q10, Q11, Q12, Q13, Q14, Q15, Q16]), "operationType" : NewBodyOperationType.REMOVE, "oppositeDirection" : true, "depth" : 25 * mm, "offsetDistance" : 25 * mm});
        }
        {
            var Q0;
            Q0=makeQuery(id+"F4.boolean.opBoolean","COPY",FACE,{"derivedFrom":makeQuery(id+"F4.opExtrude","CAP_FACE",FACE,{"disambiguationData":[OSD([sQuery(id+"F2.wireOp",EDGE,"E57.1.1"),sQuery(id+"F2.wireOp",EDGE,"E57.1.2"),sQuery(id+"F2.wireOp",EDGE,"E57.1.3"),sQuery(id+"F2.wireOp",EDGE,"E57.1.4")])],"isStart":true})});
            var Q1;
            Q1=makeQuery(id+"F4.boolean.opBoolean","COPY",FACE,{"derivedFrom":makeQuery(id+"F4.opExtrude","CAP_FACE",FACE,{"disambiguationData":[OSD([sQuery(id+"F2.wireOp",EDGE,"E57.2.1"),sQuery(id+"F2.wireOp",EDGE,"E57.2.2"),sQuery(id+"F2.wireOp",EDGE,"E57.2.3"),sQuery(id+"F2.wireOp",EDGE,"E57.2.4")])],"isStart":true})});
            var Q2;
            Q2=makeQuery(id+"F4.boolean.opBoolean","COPY",FACE,{"derivedFrom":makeQuery(id+"F4.opExtrude","CAP_FACE",FACE,{"disambiguationData":[OSD([sQuery(id+"F2.wireOp",EDGE,"E57.3.1"),sQuery(id+"F2.wireOp",EDGE,"E57.3.2"),sQuery(id+"F2.wireOp",EDGE,"E57.3.3"),sQuery(id+"F2.wireOp",EDGE,"E57.3.4")])],"isStart":true})});
            var Q3;
            Q3=makeQuery(id+"F4.boolean.opBoolean","COPY",FACE,{"derivedFrom":makeQuery(id+"F4.opExtrude","CAP_FACE",FACE,{"disambiguationData":[OSD([sQuery(id+"F2.wireOp",EDGE,"E51"),sQuery(id+"F2.wireOp",EDGE,"E52"),sQuery(id+"F2.wireOp",EDGE,"E53"),sQuery(id+"F2.wireOp",EDGE,"E54")])],"isStart":true})});
            var Q4;
            Q4=makeQuery(id+"F4.boolean.opBoolean","COPY",FACE,{"derivedFrom":makeQuery(id+"F4.opExtrude","CAP_FACE",FACE,{"disambiguationData":[OSD([sQuery(id+"F2.wireOp",EDGE,"E57.16.1"),sQuery(id+"F2.wireOp",EDGE,"E57.16.2"),sQuery(id+"F2.wireOp",EDGE,"E57.16.3"),sQuery(id+"F2.wireOp",EDGE,"E57.16.4")])],"isStart":true})});
            var Q5;
            Q5=makeQuery(id+"F4.boolean.opBoolean","COPY",FACE,{"derivedFrom":makeQuery(id+"F4.opExtrude","CAP_FACE",FACE,{"disambiguationData":[OSD([sQuery(id+"F2.wireOp",EDGE,"E57.15.1"),sQuery(id+"F2.wireOp",EDGE,"E57.15.2"),sQuery(id+"F2.wireOp",EDGE,"E57.15.3"),sQuery(id+"F2.wireOp",EDGE,"E57.15.4")])],"isStart":true})});
            var Q6;
            Q6=makeQuery(id+"F4.boolean.opBoolean","COPY",FACE,{"derivedFrom":makeQuery(id+"F4.opExtrude","CAP_FACE",FACE,{"disambiguationData":[OSD([sQuery(id+"F2.wireOp",EDGE,"E57.14.1"),sQuery(id+"F2.wireOp",EDGE,"E57.14.2"),sQuery(id+"F2.wireOp",EDGE,"E57.14.3"),sQuery(id+"F2.wireOp",EDGE,"E57.14.4")])],"isStart":true})});
            var Q7;
            Q7=makeQuery(id+"F4.boolean.opBoolean","COPY",FACE,{"derivedFrom":makeQuery(id+"F4.opExtrude","CAP_FACE",FACE,{"disambiguationData":[OSD([sQuery(id+"F2.wireOp",EDGE,"E57.13.1"),sQuery(id+"F2.wireOp",EDGE,"E57.13.2"),sQuery(id+"F2.wireOp",EDGE,"E57.13.3"),sQuery(id+"F2.wireOp",EDGE,"E57.13.4")])],"isStart":true})});
            var Q8;
            Q8=makeQuery(id+"F4.boolean.opBoolean","COPY",FACE,{"derivedFrom":makeQuery(id+"F4.opExtrude","CAP_FACE",FACE,{"disambiguationData":[OSD([sQuery(id+"F2.wireOp",EDGE,"E57.12.1"),sQuery(id+"F2.wireOp",EDGE,"E57.12.2"),sQuery(id+"F2.wireOp",EDGE,"E57.12.3"),sQuery(id+"F2.wireOp",EDGE,"E57.12.4")])],"isStart":true})});
            var Q9;
            Q9=makeQuery(id+"F4.boolean.opBoolean","COPY",FACE,{"derivedFrom":makeQuery(id+"F4.opExtrude","CAP_FACE",FACE,{"disambiguationData":[OSD([sQuery(id+"F2.wireOp",EDGE,"E57.11.1"),sQuery(id+"F2.wireOp",EDGE,"E57.11.2"),sQuery(id+"F2.wireOp",EDGE,"E57.11.3"),sQuery(id+"F2.wireOp",EDGE,"E57.11.4")])],"isStart":true})});
            var Q10;
            Q10=makeQuery(id+"F4.boolean.opBoolean","COPY",FACE,{"derivedFrom":makeQuery(id+"F4.opExtrude","CAP_FACE",FACE,{"disambiguationData":[OSD([sQuery(id+"F2.wireOp",EDGE,"E57.10.1"),sQuery(id+"F2.wireOp",EDGE,"E57.10.2"),sQuery(id+"F2.wireOp",EDGE,"E57.10.3"),sQuery(id+"F2.wireOp",EDGE,"E57.10.4")])],"isStart":true})});
            var Q11;
            Q11=makeQuery(id+"F4.boolean.opBoolean","COPY",FACE,{"derivedFrom":makeQuery(id+"F4.opExtrude","CAP_FACE",FACE,{"disambiguationData":[OSD([sQuery(id+"F2.wireOp",EDGE,"E57.4.1"),sQuery(id+"F2.wireOp",EDGE,"E57.4.2"),sQuery(id+"F2.wireOp",EDGE,"E57.4.3"),sQuery(id+"F2.wireOp",EDGE,"E57.4.4")])],"isStart":true})});
            var Q12;
            Q12=makeQuery(id+"F4.boolean.opBoolean","COPY",FACE,{"derivedFrom":makeQuery(id+"F4.opExtrude","CAP_FACE",FACE,{"disambiguationData":[OSD([sQuery(id+"F2.wireOp",EDGE,"E57.5.1"),sQuery(id+"F2.wireOp",EDGE,"E57.5.2"),sQuery(id+"F2.wireOp",EDGE,"E57.5.3"),sQuery(id+"F2.wireOp",EDGE,"E57.5.4")])],"isStart":true})});
            var Q13;
            Q13=makeQuery(id+"F4.boolean.opBoolean","COPY",FACE,{"derivedFrom":makeQuery(id+"F4.opExtrude","CAP_FACE",FACE,{"disambiguationData":[OSD([sQuery(id+"F2.wireOp",EDGE,"E57.6.1"),sQuery(id+"F2.wireOp",EDGE,"E57.6.2"),sQuery(id+"F2.wireOp",EDGE,"E57.6.3"),sQuery(id+"F2.wireOp",EDGE,"E57.6.4")])],"isStart":true})});
            var Q14;
            Q14=makeQuery(id+"F4.boolean.opBoolean","COPY",FACE,{"derivedFrom":makeQuery(id+"F4.opExtrude","CAP_FACE",FACE,{"disambiguationData":[OSD([sQuery(id+"F2.wireOp",EDGE,"E57.7.1"),sQuery(id+"F2.wireOp",EDGE,"E57.7.2"),sQuery(id+"F2.wireOp",EDGE,"E57.7.3"),sQuery(id+"F2.wireOp",EDGE,"E57.7.4")])],"isStart":true})});
            var Q15;
            Q15=makeQuery(id+"F4.boolean.opBoolean","COPY",FACE,{"derivedFrom":makeQuery(id+"F4.opExtrude","CAP_FACE",FACE,{"disambiguationData":[OSD([sQuery(id+"F2.wireOp",EDGE,"E57.8.1"),sQuery(id+"F2.wireOp",EDGE,"E57.8.2"),sQuery(id+"F2.wireOp",EDGE,"E57.8.3"),sQuery(id+"F2.wireOp",EDGE,"E57.8.4")])],"isStart":true})});
            var Q16;
            Q16=makeQuery(id+"F4.boolean.opBoolean","COPY",FACE,{"derivedFrom":makeQuery(id+"F4.opExtrude","CAP_FACE",FACE,{"disambiguationData":[OSD([sQuery(id+"F2.wireOp",EDGE,"E57.9.1"),sQuery(id+"F2.wireOp",EDGE,"E57.9.2"),sQuery(id+"F2.wireOp",EDGE,"E57.9.3"),sQuery(id+"F2.wireOp",EDGE,"E57.9.4")])],"isStart":true})});
            extrude(context, id + "F6", {"entities" : qUnion([Q0, Q1, Q2, Q3, Q4, Q5, Q6, Q7, Q8, Q9, Q10, Q11, Q12, Q13, Q14, Q15, Q16]), "operationType" : NewBodyOperationType.REMOVE, "oppositeDirection" : true, "depth" : 25 * mm, "offsetDistance" : 25 * mm});
        }
        {
            var Q0;
            Q0=makeQuery(id+"F1.opRevolve","SWEPT_FACE",FACE,{"disambiguationData":[OSD([sQuery(id+"F0.wireOp",EDGE,"E5")])]});
            var sketch = newSketch(context, id + "F7", { "sketchPlane" : qUnion([Q0])});
            skCircle(sketch, "E58", {"center": v(0, 37) * mm, "radius": 6 * mm});
            skLineSegment(sketch, "E59", {"start": v(0, 37) * mm, "end": v(0, 0) * mm, "construction": true});
            skCircle(sketch, "E60.1.0", {"center": v(-37, 0) * mm, "radius": 6 * mm});
            skCircle(sketch, "E60.2.0", {"center": v(0, -37) * mm, "radius": 6 * mm});
            skCircle(sketch, "E60.3.0", {"center": v(37, 0) * mm, "radius": 6 * mm});
            skPoint(sketch, "E60.center", {"position": v(0, 0) * mm});
            skSolve(sketch);
        }
        {
            var Q0;
            Q0=makeQuery(id+"F7.imprint","IMPRINT",FACE,{"disambiguationData":[TD([[makeQuery(id+"F7.imprint","IMPRINT",EDGE,{"derivedFrom":sQuery(id+"F7.wireOp",EDGE,"E60.1.0")}),1.0]])]});
            var Q1;
            Q1=makeQuery(id+"F7.imprint","IMPRINT",FACE,{"disambiguationData":[TD([[makeQuery(id+"F7.imprint","IMPRINT",EDGE,{"derivedFrom":sQuery(id+"F7.wireOp",EDGE,"E58")}),1.0]])]});
            var Q2;
            Q2=makeQuery(id+"F7.imprint","IMPRINT",FACE,{"disambiguationData":[TD([[makeQuery(id+"F7.imprint","IMPRINT",EDGE,{"derivedFrom":sQuery(id+"F7.wireOp",EDGE,"E60.3.0")}),1.0]])]});
            var Q3;
            Q3=makeQuery(id+"F7.imprint","IMPRINT",FACE,{"disambiguationData":[TD([[makeQuery(id+"F7.imprint","IMPRINT",EDGE,{"derivedFrom":sQuery(id+"F7.wireOp",EDGE,"E60.2.0")}),1.0]])]});
            extrude(context, id + "F8", {"entities" : qUnion([Q0, Q1, Q2, Q3]), "operationType" : NewBodyOperationType.REMOVE, "oppositeDirection" : true, "depth" : 200 * mm, "offsetDistance" : 25 * mm});
        }
    });
